# Revit family: GP212-sw
name_source: partatom
category: Communication Devices
revit_build: Autodesk Revit Architecture 2012 (Build: 20110309_2315(x64)
units: mm (PartAtom-declared; Revit-internal decimal feet)

## types (1)
- GP212-sw
    Default Elevation = 0.000"
    Depth = 29.000"
    Description = Dual 12" Bandpass Subwoofer
    Enclosure Material = Black Finish
    Height = 15.000"
    Impedance = 4
    Manufacturer = QSC Audio Products, LLC
    Manufacturer URL = www.qscaudio.com
    Model = GP212-sw
    Power Handling = 1100
    Product Documentation Link = http://media.qscaudio.com
    Product Page URL = http://www.qscaudio.com
    Regulatory Compliance = RoHS
    SPL Max = 135.4
    Sensitivity = 99
    URL = http://www.qscaudio.com
    Vent Depth = -28.250"
    Weight Dimensional (kg) = 52.4
    Weight Dimensional (lb) = 115.5
    Weight Product (kg) = 45.1
    Weight Product (lb) = 99.5
    Width = 20.000"

## geometry (parser evidence)
native form markers: Blend x1, Sweep x1
no freeform markers — native parametric forms only
